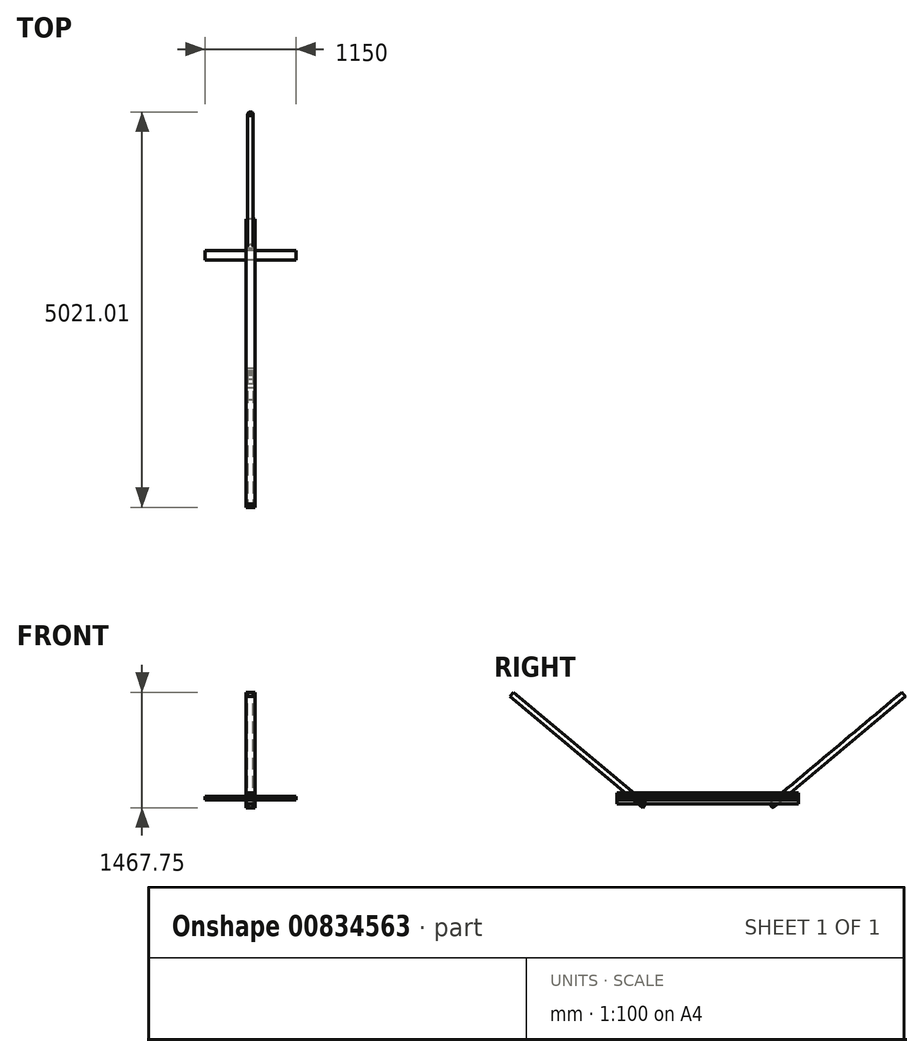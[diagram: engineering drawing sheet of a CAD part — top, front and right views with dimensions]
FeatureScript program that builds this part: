
annotation { "Feature Type Name" : "Feature", "Feature Type Description" : "" }
export const myFeature = defineFeature(function(context is Context, id is Id, definition is map)
    precondition{}
    {
        {
            var Q0;
            Q0=qCreatedBy(makeId("Right.planeOp"),FACE);
            var sketch = newSketch(context, id + "F0", { "sketchPlane" : qUnion([Q0])});
            skLineSegment(sketch, "E0.bottom", {"start": v(-380.97, 45) * mm, "end": v(1919.03, 45) * mm});
            skLineSegment(sketch, "E0.top", {"start": v(-380.97, 0) * mm, "end": v(1919.03, 0) * mm});
            skLineSegment(sketch, "E0.left", {"start": v(-380.97, 45) * mm, "end": v(-380.97, 0) * mm});
            skLineSegment(sketch, "E0.right", {"start": v(1919.03, 45) * mm, "end": v(1919.03, 0) * mm});
            skLineSegment(sketch, "E1.bottom", {"start": v(-56.18, -53.62) * mm, "end": v(-1741.48, 1360.5) * mm});
            skLineSegment(sketch, "E1.top", {"start": v(-11.18, 0) * mm, "end": v(-1696.48, 1414.13) * mm});
            skLineSegment(sketch, "E1.left", {"start": v(-56.18, -53.62) * mm, "end": v(-11.18, 0) * mm});
            skLineSegment(sketch, "E1.right", {"start": v(-1741.48, 1360.5) * mm, "end": v(-1696.48, 1414.13) * mm});
            skPoint(sketch, "E1.middle", {"position": v(-214.17, 95.5) * mm});
            skLineSegment(sketch, "E2", {"start": v(769.03, 45) * mm, "end": v(769.03, 1678.34) * mm, "construction": true});
            skPoint(sketch, "E3.MirrorP", {"position": v(1752.23, 95.5) * mm});
            skLineSegment(sketch, "E4.bottom", {"start": v(-380.97, 90) * mm, "end": v(1919.03, 90) * mm});
            skLineSegment(sketch, "E4.top", {"start": v(-380.97, 135) * mm, "end": v(1919.03, 135) * mm});
            skLineSegment(sketch, "E4.left", {"start": v(-380.97, 90) * mm, "end": v(-380.97, 135) * mm});
            skLineSegment(sketch, "E4.right", {"start": v(1919.03, 90) * mm, "end": v(1919.03, 135) * mm});
            skLineSegment(sketch, "E5.bottom", {"start": v(-380.97, 90) * mm, "end": v(19.03, 90) * mm});
            skLineSegment(sketch, "E5.top", {"start": v(-380.97, 45) * mm, "end": v(19.03, 45) * mm});
            skLineSegment(sketch, "E5.left", {"start": v(-380.97, 90) * mm, "end": v(-380.97, 45) * mm});
            skLineSegment(sketch, "E5.right", {"start": v(19.03, 90) * mm, "end": v(19.03, 45) * mm});
            skPoint(sketch, "E6", {"position": v(-280.97, 135) * mm});
            skLineSegment(sketch, "E7.MirrorCS", {"start": v(1549.24, 0) * mm, "end": v(3234.54, 1414.13) * mm});
            skLineSegment(sketch, "E8.MirrorCS", {"start": v(1594.24, -53.62) * mm, "end": v(3279.53, 1360.5) * mm});
            skLineSegment(sketch, "E9.MirrorCS", {"start": v(3279.53, 1360.5) * mm, "end": v(3234.54, 1414.13) * mm});
            skLineSegment(sketch, "E10.MirrorCS", {"start": v(1594.24, -53.62) * mm, "end": v(1549.24, 0) * mm});
            skLineSegment(sketch, "E11.MirrorCS", {"start": v(1519.03, 90) * mm, "end": v(1519.03, 45) * mm});
            skLineSegment(sketch, "E12.MirrorCS", {"start": v(1919.03, 90) * mm, "end": v(1919.03, 45) * mm});
            skPoint(sketch, "E13.MirrorP", {"position": v(1819.03, 135) * mm});
            skLineSegment(sketch, "E14.bottom", {"start": v(19.03, 90) * mm, "end": v(139.03, 90) * mm});
            skLineSegment(sketch, "E14.top", {"start": v(19.03, 45) * mm, "end": v(139.03, 45) * mm});
            skLineSegment(sketch, "E14.right", {"start": v(139.03, 90) * mm, "end": v(139.03, 45) * mm});
            skLineSegment(sketch, "E15.MirrorCS", {"start": v(1399.03, 90) * mm, "end": v(1399.03, 45) * mm});
            skLineSegment(sketch, "E16", {"start": v(-1718.98, 1387.32) * mm, "end": v(-33.68, -26.81) * mm});
            skLineSegment(sketch, "E17.MirrorCS", {"start": v(3257.04, 1387.32) * mm, "end": v(1571.74, -26.81) * mm});
            skPoint(sketch, "E18", {"position": v(-226.52, 135) * mm});
            skSolve(sketch);
        }
        {
            var Q0;
            {var subQ0=sQuery(id+"F0.wireOp",EDGE,"E4.right");Q0=makeQuery(id+"F0.imprint","IMPRINT",FACE,{"disambiguationData":[TD([[makeQuery(id+"F0.imprint","IMPRINT",EDGE,{"derivedFrom":subQ0}),1.0]])]});}
            var Q1;
            {var subQ0=sQuery(id+"F0.wireOp",EDGE,"E4.top");var subQ1=sQuery(id+"F0.wireOp",EDGE,"E1.bottom");var subQ2=makeQuery(id+"F0.imprint","INTERSECT",VERTEX,{"derivedFrom":[subQ1,subQ0]});Q1=makeQuery(id+"F0.imprint","IMPRINT",FACE,{"disambiguationData":[TD([[makeQuery(id+"F0.imprint","IMPRINT",EDGE,{"disambiguationData":[TD([[subQ2,1.0]])],"derivedFrom":subQ1}),-1.0]])]});}
            var Q2;
            {var subQ0=sQuery(id+"F0.wireOp",EDGE,"E7.MirrorCS");var subQ1=sQuery(id+"F0.wireOp",EDGE,"E4.bottom");var subQ2=makeQuery(id+"F0.imprint","INTERSECT",VERTEX,{"derivedFrom":[subQ1,subQ0]});Q2=makeQuery(id+"F0.imprint","IMPRINT",FACE,{"disambiguationData":[TD([[makeQuery(id+"F0.imprint","IMPRINT",EDGE,{"disambiguationData":[TD([[subQ2,-1.0]])],"derivedFrom":subQ1}),1.0]])]});}
            var Q3;
            {var subQ5=sQuery(id+"F0.wireOp",EDGE,"E4.left");Q3=makeQuery(id+"F0.imprint","IMPRINT",FACE,{"disambiguationData":[TD([[makeQuery(id+"F0.imprint","IMPRINT",EDGE,{"derivedFrom":subQ5}),-1.0]])]});}
            var Q4;
            {var subQ0=sQuery(id+"F0.wireOp",EDGE,"E4.top");var subQ1=sQuery(id+"F0.wireOp",EDGE,"E1.top");var subQ2=makeQuery(id+"F0.imprint","INTERSECT",VERTEX,{"derivedFrom":[subQ1,subQ0]});Q4=makeQuery(id+"F0.imprint","IMPRINT",FACE,{"disambiguationData":[TD([[makeQuery(id+"F0.imprint","IMPRINT",EDGE,{"disambiguationData":[TD([[subQ2,1.0]])],"derivedFrom":subQ1}),-1.0]])]});}
            var Q5;
            {var subQ0=sQuery(id+"F0.wireOp",EDGE,"E4.top");var subQ1=sQuery(id+"F0.wireOp",EDGE,"E1.top");var subQ2=makeQuery(id+"F0.imprint","INTERSECT",VERTEX,{"derivedFrom":[subQ1,subQ0]});Q5=makeQuery(id+"F0.imprint","IMPRINT",FACE,{"disambiguationData":[TD([[makeQuery(id+"F0.imprint","IMPRINT",EDGE,{"disambiguationData":[TD([[subQ2,1.0]])],"derivedFrom":subQ1}),1.0]])]});}
            var Q6;
            {var subQ0=sQuery(id+"F0.wireOp",EDGE,"E17.MirrorCS");var subQ1=sQuery(id+"F0.wireOp",EDGE,"E4.bottom");var subQ2=makeQuery(id+"F0.imprint","INTERSECT",VERTEX,{"derivedFrom":[subQ1,subQ0]});Q6=makeQuery(id+"F0.imprint","IMPRINT",FACE,{"disambiguationData":[TD([[makeQuery(id+"F0.imprint","IMPRINT",EDGE,{"disambiguationData":[TD([[subQ2,-1.0]])],"derivedFrom":subQ1}),1.0]])]});}
            extrude(context, id + "F1", {"entities" : qUnion([Q0, Q1, Q2, Q3, Q4, Q5, Q6]), "depth" : 120 * mm, "offsetDistance" : 25 * mm});
        }
        {
            var Q0;
            {var subQ0=sQuery(id+"F0.wireOp",EDGE,"E0.left");Q0=makeQuery(id+"F0.imprint","IMPRINT",FACE,{"disambiguationData":[TD([[makeQuery(id+"F0.imprint","IMPRINT",EDGE,{"derivedFrom":subQ0}),1.0]])]});}
            var Q1;
            {var subQ1=sQuery(id+"F0.wireOp",EDGE,"E0.top");var subQ3=sQuery(id+"F0.wireOp",EDGE,"E1.bottom");var subQ4=makeQuery(id+"F0.imprint","INTERSECT",VERTEX,{"derivedFrom":[subQ1,subQ3]});Q1=makeQuery(id+"F0.imprint","IMPRINT",FACE,{"disambiguationData":[TD([[makeQuery(id+"F0.imprint","IMPRINT",EDGE,{"disambiguationData":[TD([[subQ4,-1.0]])],"derivedFrom":subQ3}),-1.0]])]});}
            var Q2;
            {var subQ0=sQuery(id+"F0.wireOp",EDGE,"E0.right");Q2=makeQuery(id+"F0.imprint","IMPRINT",FACE,{"disambiguationData":[TD([[makeQuery(id+"F0.imprint","IMPRINT",EDGE,{"derivedFrom":subQ0}),-1.0]])]});}
            var Q3;
            {var subQ7=sQuery(id+"F0.wireOp",EDGE,"E0.bottom");var subQ8=makeQuery(id+"F0.imprint","INTERSECT",VERTEX,{"derivedFrom":[subQ7,sQuery(id+"F0.wireOp",EDGE,"E11.MirrorCS")]});Q3=makeQuery(id+"F0.imprint","IMPRINT",FACE,{"disambiguationData":[TD([[makeQuery(id+"F0.imprint","IMPRINT",EDGE,{"disambiguationData":[TD([[subQ8,-1.0]])],"derivedFrom":subQ7}),-1.0]])]});}
            var Q4;
            {var subQ0=sQuery(id+"F0.wireOp",EDGE,"E7.MirrorCS");var subQ1=sQuery(id+"F0.wireOp",EDGE,"E0.bottom");var subQ2=makeQuery(id+"F0.imprint","INTERSECT",VERTEX,{"derivedFrom":[subQ1,subQ0]});Q4=makeQuery(id+"F0.imprint","IMPRINT",FACE,{"disambiguationData":[TD([[makeQuery(id+"F0.imprint","IMPRINT",EDGE,{"disambiguationData":[TD([[subQ2,-1.0]])],"derivedFrom":subQ1}),-1.0]])]});}
            var Q5;
            {var subQ0=sQuery(id+"F0.wireOp",EDGE,"E17.MirrorCS");var subQ1=sQuery(id+"F0.wireOp",EDGE,"E0.bottom");var subQ2=makeQuery(id+"F0.imprint","INTERSECT",VERTEX,{"derivedFrom":[subQ1,subQ0]});Q5=makeQuery(id+"F0.imprint","IMPRINT",FACE,{"disambiguationData":[TD([[makeQuery(id+"F0.imprint","IMPRINT",EDGE,{"disambiguationData":[TD([[subQ2,-1.0]])],"derivedFrom":subQ1}),-1.0]])]});}
            var Q6;
            {var subQ0=sQuery(id+"F0.wireOp",EDGE,"E1.top");var subQ5=sQuery(id+"F0.wireOp",EDGE,"E5.top");var subQ6=makeQuery(id+"F0.imprint","INTERSECT",VERTEX,{"derivedFrom":[subQ0,subQ5]});Q6=makeQuery(id+"F0.imprint","IMPRINT",FACE,{"disambiguationData":[TD([[makeQuery(id+"F0.imprint","IMPRINT",EDGE,{"disambiguationData":[TD([[subQ6,1.0]])],"derivedFrom":subQ5}),-1.0]])]});}
            extrude(context, id + "F2", {"entities" : qUnion([Q0, Q1, Q2, Q3, Q4, Q5, Q6]), "depth" : 120 * mm, "offsetDistance" : 25 * mm});
        }
        {
            var Q0;
            {var subQ5=sQuery(id+"F0.wireOp",EDGE,"E5.left");Q0=makeQuery(id+"F0.imprint","IMPRINT",FACE,{"disambiguationData":[TD([[makeQuery(id+"F0.imprint","IMPRINT",EDGE,{"derivedFrom":subQ5}),1.0]])]});}
            var Q1;
            {var subQ0=sQuery(id+"F0.wireOp",EDGE,"E5.top");var subQ1=sQuery(id+"F0.wireOp",EDGE,"E1.bottom");var subQ2=makeQuery(id+"F0.imprint","INTERSECT",VERTEX,{"derivedFrom":[subQ1,subQ0]});Q1=makeQuery(id+"F0.imprint","IMPRINT",FACE,{"disambiguationData":[TD([[makeQuery(id+"F0.imprint","IMPRINT",EDGE,{"disambiguationData":[TD([[subQ2,-1.0]])],"derivedFrom":subQ1}),-1.0]])]});}
            var Q2;
            {var subQ0=sQuery(id+"F0.wireOp",EDGE,"E5.top");var subQ1=sQuery(id+"F0.wireOp",EDGE,"E1.top");var subQ2=makeQuery(id+"F0.imprint","INTERSECT",VERTEX,{"derivedFrom":[subQ1,subQ0]});Q2=makeQuery(id+"F0.imprint","IMPRINT",FACE,{"disambiguationData":[TD([[makeQuery(id+"F0.imprint","IMPRINT",EDGE,{"disambiguationData":[TD([[subQ2,-1.0]])],"derivedFrom":subQ1}),1.0]])]});}
            var Q3;
            {var subQ5=sQuery(id+"F0.wireOp",EDGE,"E5.right");Q3=makeQuery(id+"F0.imprint","IMPRINT",FACE,{"disambiguationData":[TD([[makeQuery(id+"F0.imprint","IMPRINT",EDGE,{"derivedFrom":subQ5}),-1.0]])]});}
            var Q4;
            {var subQ0=sQuery(id+"F0.wireOp",EDGE,"E11.MirrorCS");Q4=makeQuery(id+"F0.imprint","IMPRINT",FACE,{"disambiguationData":[TD([[makeQuery(id+"F0.imprint","IMPRINT",EDGE,{"derivedFrom":subQ0}),1.0]])]});}
            var Q5;
            {var subQ0=sQuery(id+"F0.wireOp",EDGE,"E7.MirrorCS");var subQ1=sQuery(id+"F0.wireOp",EDGE,"E0.bottom");var subQ2=makeQuery(id+"F0.imprint","INTERSECT",VERTEX,{"derivedFrom":[subQ1,subQ0]});Q5=makeQuery(id+"F0.imprint","IMPRINT",FACE,{"disambiguationData":[TD([[makeQuery(id+"F0.imprint","IMPRINT",EDGE,{"disambiguationData":[TD([[subQ2,-1.0]])],"derivedFrom":subQ1}),1.0]])]});}
            var Q6;
            {var subQ0=sQuery(id+"F0.wireOp",EDGE,"E17.MirrorCS");var subQ1=sQuery(id+"F0.wireOp",EDGE,"E0.bottom");var subQ2=makeQuery(id+"F0.imprint","INTERSECT",VERTEX,{"derivedFrom":[subQ1,subQ0]});Q6=makeQuery(id+"F0.imprint","IMPRINT",FACE,{"disambiguationData":[TD([[makeQuery(id+"F0.imprint","IMPRINT",EDGE,{"disambiguationData":[TD([[subQ2,-1.0]])],"derivedFrom":subQ1}),1.0]])]});}
            var Q7;
            {var subQ0=sQuery(id+"F0.wireOp",EDGE,"E12.MirrorCS");Q7=makeQuery(id+"F0.imprint","IMPRINT",FACE,{"disambiguationData":[TD([[makeQuery(id+"F0.imprint","IMPRINT",EDGE,{"derivedFrom":subQ0}),-1.0]])]});}
            extrude(context, id + "F3", {"entities" : qUnion([Q0, Q1, Q2, Q3, Q4, Q5, Q6, Q7]), "depth" : 120 * mm, "offsetDistance" : 25 * mm});
        }
        {
            var Q0;
            Q0=makeQuery(id+"F0.imprint","IMPRINT",FACE,{"disambiguationData":[TD([[makeQuery(id+"F0.imprint","IMPRINT",EDGE,{"derivedFrom":sQuery(id+"F0.wireOp",EDGE,"E14.bottom")}),-1.0]])]});
            var Q1;
            {var subQ0=sQuery(id+"F0.wireOp",EDGE,"E11.MirrorCS");Q1=makeQuery(id+"F0.imprint","IMPRINT",FACE,{"disambiguationData":[TD([[makeQuery(id+"F0.imprint","IMPRINT",EDGE,{"derivedFrom":subQ0}),-1.0]])]});}
            extrude(context, id + "F4", {"entities" : qUnion([Q0, Q1]), "depth" : 1150 * mm, "offsetDistance" : 25 * mm});
        }
        {
            var Q0;
            Q0=makeQuery(id+"F4.opExtrude","SWEPT_BODY",BODY,{"disambiguationData":[OSD([sQuery(id+"F0.wireOp",EDGE,"E0.bottom"),sQuery(id+"F0.wireOp",EDGE,"E4.bottom"),sQuery(id+"F0.wireOp",EDGE,"E11.MirrorCS"),sQuery(id+"F0.wireOp",EDGE,"E15.MirrorCS")])]});
            var Q1;
            Q1=makeQuery(id+"F4.opExtrude","SWEPT_BODY",BODY,{"disambiguationData":[OSD([sQuery(id+"F0.wireOp",EDGE,"E14.bottom"),sQuery(id+"F0.wireOp",EDGE,"E14.top"),sQuery(id+"F0.wireOp",EDGE,"E5.right"),sQuery(id+"F0.wireOp",EDGE,"E14.right")])]});
            var Q2;
            Q2=makeQuery(id+"F4.opExtrude","SWEPT_EDGE",EDGE,{"disambiguationData":[OSD([sQuery(id+"F0.wireOp",EDGE,"E0.bottom"),sQuery(id+"F0.wireOp",EDGE,"E15.MirrorCS")])]});
            var Q3;
            Q3=makeQuery(id+"F4.opExtrude","SWEPT_EDGE",EDGE,{"disambiguationData":[OSD([sQuery(id+"F0.wireOp",EDGE,"E0.bottom"),sQuery(id+"F0.wireOp",EDGE,"E15.MirrorCS")])]});
            transform(context, id + "F5", {"entities" : qUnion([Q0, Q1]), "transformType" : TransformType.TRANSLATION_DISTANCE, "transformDirection" : qUnion([Q3]), "distance" : 515 * mm, "makeCopy" : false});
        }
        {
            var Q0;
            {var subQ0=sQuery(id+"F0.wireOp",EDGE,"E4.top");var subQ1=sQuery(id+"F0.wireOp",EDGE,"E1.bottom");var subQ2=makeQuery(id+"F0.imprint","INTERSECT",VERTEX,{"derivedFrom":[subQ1,subQ0]});Q0=makeQuery(id+"F0.imprint","IMPRINT",FACE,{"disambiguationData":[TD([[makeQuery(id+"F0.imprint","IMPRINT",EDGE,{"disambiguationData":[TD([[subQ2,1.0]])],"derivedFrom":subQ1}),-1.0]])]});}
            var Q1;
            {var subQ0=sQuery(id+"F0.wireOp",EDGE,"E5.top");var subQ1=sQuery(id+"F0.wireOp",EDGE,"E1.bottom");var subQ2=makeQuery(id+"F0.imprint","INTERSECT",VERTEX,{"derivedFrom":[subQ1,subQ0]});Q1=makeQuery(id+"F0.imprint","IMPRINT",FACE,{"disambiguationData":[TD([[makeQuery(id+"F0.imprint","IMPRINT",EDGE,{"disambiguationData":[TD([[subQ2,-1.0]])],"derivedFrom":subQ1}),-1.0]])]});}
            var Q2;
            {var subQ1=sQuery(id+"F0.wireOp",EDGE,"E0.top");var subQ3=sQuery(id+"F0.wireOp",EDGE,"E1.bottom");var subQ4=makeQuery(id+"F0.imprint","INTERSECT",VERTEX,{"derivedFrom":[subQ1,subQ3]});Q2=makeQuery(id+"F0.imprint","IMPRINT",FACE,{"disambiguationData":[TD([[makeQuery(id+"F0.imprint","IMPRINT",EDGE,{"disambiguationData":[TD([[subQ4,-1.0]])],"derivedFrom":subQ3}),-1.0]])]});}
            var Q3;
            {var subQ0=sQuery(id+"F0.wireOp",EDGE,"E1.bottom");var subQ1=sQuery(id+"F0.wireOp",EDGE,"E0.top");var subQ2=makeQuery(id+"F0.imprint","INTERSECT",VERTEX,{"derivedFrom":[subQ1,subQ0]});Q3=makeQuery(id+"F0.imprint","IMPRINT",FACE,{"disambiguationData":[TD([[makeQuery(id+"F0.imprint","IMPRINT",EDGE,{"disambiguationData":[TD([[subQ2,-1.0]])],"derivedFrom":subQ1}),-1.0]])]});}
            var Q4;
            {var subQ0=sQuery(id+"F0.wireOp",EDGE,"E1.right");var subQ1=sQuery(id+"F0.wireOp",EDGE,"E1.bottom");var subQ2=makeQuery(id+"F0.imprint","INTERSECT",VERTEX,{"derivedFrom":[subQ1,subQ0]});Q4=makeQuery(id+"F0.imprint","IMPRINT",FACE,{"disambiguationData":[TD([[makeQuery(id+"F0.imprint","IMPRINT",EDGE,{"disambiguationData":[TD([[subQ2,1.0]])],"derivedFrom":subQ1}),-1.0]])]});}
            var Q5;
            Q5=sQuery(id+"F0.wireOp",EDGE,"E16");
            revolve(context, id + "F6", {"surfaceOperationType" : NewSurfaceOperationType.NEW, "entities" : qUnion([Q0, Q1, Q2, Q3, Q4]), "axis" : qUnion([Q5]), "revolveType" : RevolveType.FULL});
        }
        {
            var Q0;
            {var subQ0=sQuery(id+"F0.wireOp",EDGE,"E8.MirrorCS");var subQ1=sQuery(id+"F0.wireOp",EDGE,"E0.top");var subQ2=makeQuery(id+"F0.imprint","INTERSECT",VERTEX,{"derivedFrom":[subQ1,subQ0]});Q0=makeQuery(id+"F0.imprint","IMPRINT",FACE,{"disambiguationData":[TD([[makeQuery(id+"F0.imprint","IMPRINT",EDGE,{"disambiguationData":[TD([[subQ2,1.0]])],"derivedFrom":subQ1}),-1.0]])]});}
            var Q1;
            {var subQ0=sQuery(id+"F0.wireOp",EDGE,"E17.MirrorCS");var subQ1=sQuery(id+"F0.wireOp",EDGE,"E0.bottom");var subQ2=makeQuery(id+"F0.imprint","INTERSECT",VERTEX,{"derivedFrom":[subQ1,subQ0]});Q1=makeQuery(id+"F0.imprint","IMPRINT",FACE,{"disambiguationData":[TD([[makeQuery(id+"F0.imprint","IMPRINT",EDGE,{"disambiguationData":[TD([[subQ2,-1.0]])],"derivedFrom":subQ1}),-1.0]])]});}
            var Q2;
            {var subQ0=sQuery(id+"F0.wireOp",EDGE,"E17.MirrorCS");var subQ1=sQuery(id+"F0.wireOp",EDGE,"E0.bottom");var subQ2=makeQuery(id+"F0.imprint","INTERSECT",VERTEX,{"derivedFrom":[subQ1,subQ0]});Q2=makeQuery(id+"F0.imprint","IMPRINT",FACE,{"disambiguationData":[TD([[makeQuery(id+"F0.imprint","IMPRINT",EDGE,{"disambiguationData":[TD([[subQ2,-1.0]])],"derivedFrom":subQ1}),1.0]])]});}
            var Q3;
            {var subQ0=sQuery(id+"F0.wireOp",EDGE,"E17.MirrorCS");var subQ1=sQuery(id+"F0.wireOp",EDGE,"E4.bottom");var subQ2=makeQuery(id+"F0.imprint","INTERSECT",VERTEX,{"derivedFrom":[subQ1,subQ0]});Q3=makeQuery(id+"F0.imprint","IMPRINT",FACE,{"disambiguationData":[TD([[makeQuery(id+"F0.imprint","IMPRINT",EDGE,{"disambiguationData":[TD([[subQ2,-1.0]])],"derivedFrom":subQ1}),1.0]])]});}
            var Q4;
            {var subQ0=sQuery(id+"F0.wireOp",EDGE,"E8.MirrorCS");var subQ1=sQuery(id+"F0.wireOp",EDGE,"E4.top");var subQ2=makeQuery(id+"F0.imprint","INTERSECT",VERTEX,{"derivedFrom":[subQ1,subQ0]});Q4=makeQuery(id+"F0.imprint","IMPRINT",FACE,{"disambiguationData":[TD([[makeQuery(id+"F0.imprint","IMPRINT",EDGE,{"disambiguationData":[TD([[subQ2,1.0]])],"derivedFrom":subQ1}),1.0]])]});}
            var Q5;
            Q5=sQuery(id+"F0.wireOp",EDGE,"E17.MirrorCS");
            revolve(context, id + "F7", {"surfaceOperationType" : NewSurfaceOperationType.NEW, "entities" : qUnion([Q0, Q1, Q2, Q3, Q4]), "axis" : qUnion([Q5]), "revolveType" : RevolveType.FULL});
        }
        {
            var Q0;
            Q0=makeQuery(id+"F6.opRevolve","SWEPT_BODY",BODY,{"disambiguationData":[OSD([sQuery(id+"F0.wireOp",EDGE,"E1.bottom"),sQuery(id+"F0.wireOp",EDGE,"E1.left"),sQuery(id+"F0.wireOp",EDGE,"E1.right"),sQuery(id+"F0.wireOp",EDGE,"E16")])]});
            var Q1;
            Q1=makeQuery(id+"F7.opRevolve","SWEPT_BODY",BODY,{"disambiguationData":[OSD([sQuery(id+"F0.wireOp",EDGE,"E8.MirrorCS"),sQuery(id+"F0.wireOp",EDGE,"E9.MirrorCS"),sQuery(id+"F0.wireOp",EDGE,"E10.MirrorCS"),sQuery(id+"F0.wireOp",EDGE,"E17.MirrorCS")])]});
            var Q2;
            Q2=makeQuery(id+"F1.opExtrude","SWEPT_EDGE",EDGE,{"disambiguationData":[OSD([sQuery(id+"F0.wireOp",EDGE,"E4.top"),sQuery(id+"F0.wireOp",EDGE,"E4.left")])]});
            transform(context, id + "F8", {"entities" : qUnion([Q0, Q1]), "transformType" : TransformType.TRANSLATION_DISTANCE, "transformDirection" : qUnion([Q2]), "distance" : 60 * mm, "oppositeDirection" : true, "makeCopy" : false});
        }
    });
